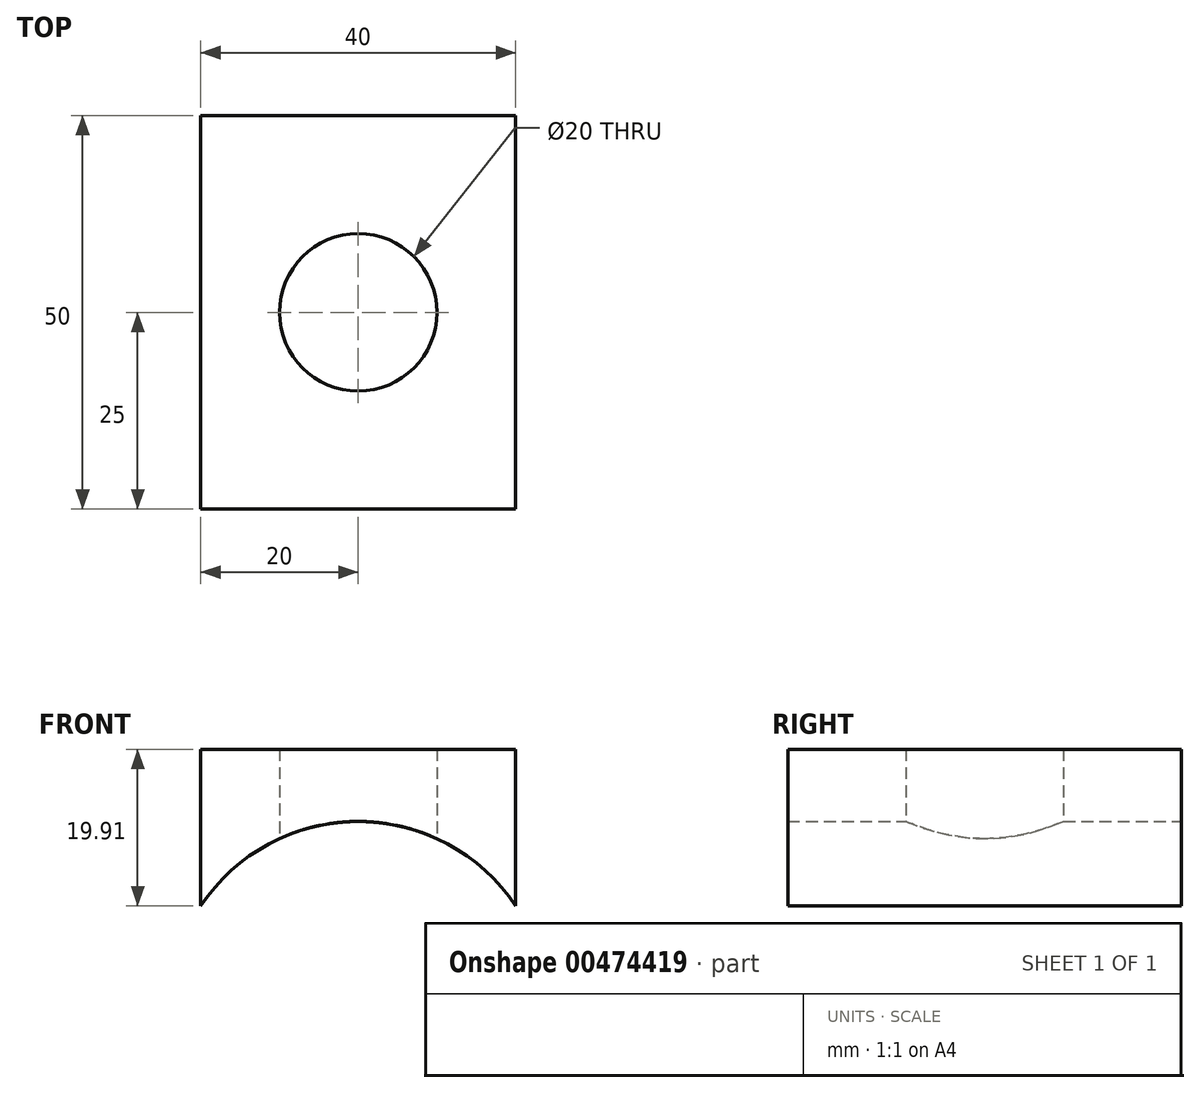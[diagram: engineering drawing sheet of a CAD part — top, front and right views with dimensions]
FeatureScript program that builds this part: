
annotation { "Feature Type Name" : "Feature", "Feature Type Description" : "" }
export const myFeature = defineFeature(function(context is Context, id is Id, definition is map)
    precondition{}
    {
        {
            var Q0;
            Q0=qCreatedBy(makeId("Front.planeOp"),FACE);
            var sketch = newSketch(context, id + "F0", { "sketchPlane" : qUnion([Q0])});
            skLineSegment(sketch, "E0.bottom", {"start": v(-20, 19.91) * mm, "end": v(20, 19.91) * mm});
            skLineSegment(sketch, "E0.top", {"start": v(-20, -0.09) * mm, "end": v(20, -0.09) * mm});
            skLineSegment(sketch, "E0.left", {"start": v(-20, 19.91) * mm, "end": v(-20, -0.09) * mm});
            skLineSegment(sketch, "E0.right", {"start": v(20, 19.91) * mm, "end": v(20, -0.09) * mm});
            skSolve(sketch);
        }
        {
            var Q0;
            Q0=qSketchRegion(id+"F0",true);
            extrude(context, id + "F1", {"entities" : qUnion([Q0]), "depth" : 50 * mm});
        }
        {
            var Q0;
            Q0=qCreatedBy(makeId("Front.planeOp"),FACE);
            var sketch = newSketch(context, id + "F2", { "sketchPlane" : qUnion([Q0])});
            skCircle(sketch, "E1", {"center": v(0, -13.27) * mm, "radius": 24 * mm});
            skPoint(sketch, "E1.first.point", {"position": v(20, 0) * mm});
            skPoint(sketch, "E1.second.point", {"position": v(0, 10.73) * mm});
            skPoint(sketch, "E1.third.point", {"position": v(-20, 0) * mm});
            skSolve(sketch);
        }
        {
            var Q0;
            Q0=qSketchRegion(id+"F2",true);
            extrude(context, id + "F3", {"entities" : qUnion([Q0]), "operationType" : NewBodyOperationType.REMOVE, "endBound" : BoundingType.THROUGH_ALL, "depth" : 25 * mm});
        }
        {
            var Q0;
            Q0=qCreatedBy(makeId("Top.planeOp"),FACE);
            var sketch = newSketch(context, id + "F4", { "sketchPlane" : qUnion([Q0])});
            skCircle(sketch, "E2", {"center": v(0, -25) * mm, "radius": 10 * mm});
            skSolve(sketch);
        }
        {
            var Q0;
            Q0=qSketchRegion(id+"F4",true);
            extrude(context, id + "F5", {"entities" : qUnion([Q0]), "operationType" : NewBodyOperationType.REMOVE, "endBound" : BoundingType.THROUGH_ALL, "depth" : 25 * mm});
        }
    });
